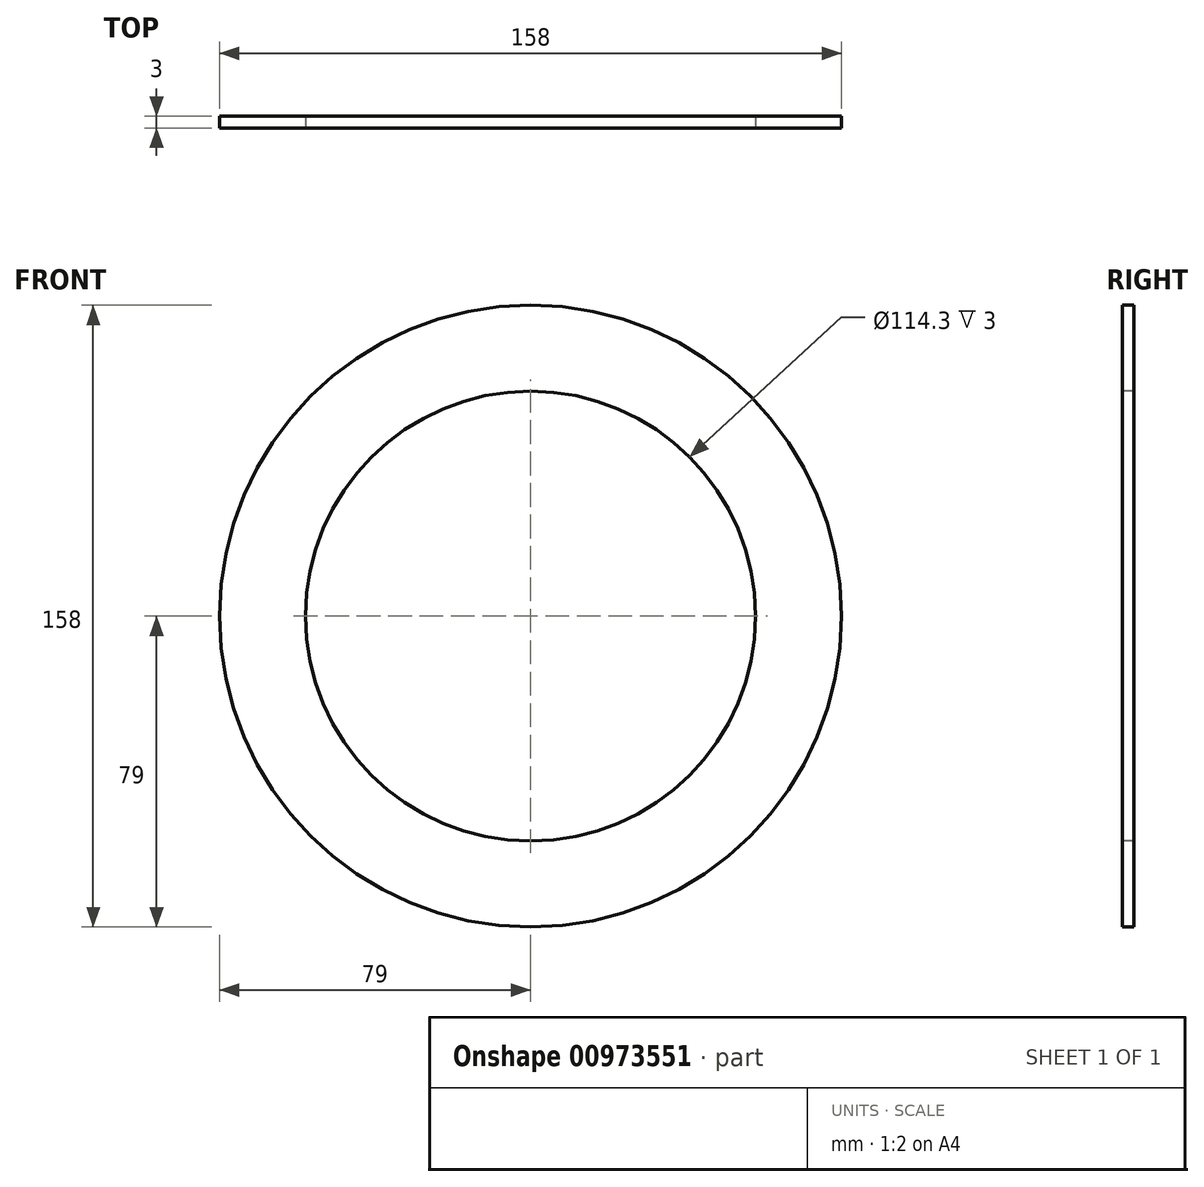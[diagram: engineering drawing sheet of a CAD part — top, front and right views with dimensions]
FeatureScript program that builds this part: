
annotation { "Feature Type Name" : "Feature", "Feature Type Description" : "" }
export const myFeature = defineFeature(function(context is Context, id is Id, definition is map)
    precondition{}
    {
        {
            var Q0;
            Q0=qCreatedBy(makeId("Front.planeOp"),FACE);
            var sketch = newSketch(context, id + "F0", { "sketchPlane" : qUnion([Q0])});
            skCircle(sketch, "E0", {"center": v(0, 0) * mm, "radius": 110 * mm});
            skCircle(sketch, "E1", {"center": v(0, 0) * mm, "radius": 79 * mm});
            skLineSegment(sketch, "E2", {"start": v(0, 0) * mm, "end": v(90, 0) * mm});
            skCircle(sketch, "E3", {"center": v(90, 0) * mm, "radius": 9 * mm});
            skPoint(sketch, "E4.center", {"position": v(41.73, 29.53) * mm});
            skCircle(sketch, "E5.1.0", {"center": v(63.64, 63.64) * mm, "radius": 9 * mm});
            skCircle(sketch, "E5.2.0", {"center": v(0, 90) * mm, "radius": 9 * mm});
            skCircle(sketch, "E5.3.0", {"center": v(-63.64, 63.64) * mm, "radius": 9 * mm});
            skCircle(sketch, "E5.4.0", {"center": v(-90, 0) * mm, "radius": 9 * mm});
            skCircle(sketch, "E5.5.0", {"center": v(-63.64, -63.64) * mm, "radius": 9 * mm});
            skCircle(sketch, "E5.6.0", {"center": v(0, -90) * mm, "radius": 9 * mm});
            skCircle(sketch, "E5.7.0", {"center": v(63.64, -63.64) * mm, "radius": 9 * mm});
            skCircle(sketch, "E6", {"center": v(0, 0) * mm, "radius": 57.15 * mm});
            skSolve(sketch);
        }
        {
            var Q0;
            Q0=makeQuery(id+"F0.imprint","IMPRINT",FACE,{"disambiguationData":[TD([[makeQuery(id+"F0.imprint","IMPRINT",EDGE,{"derivedFrom":sQuery(id+"F0.wireOp",EDGE,"E1")}),1.0]])]});
            var Q1;
            Q1=sQuery(id+"F0.wireOp",EDGE,"E1");
            var Q2;
            Q2=sQuery(id+"F0.wireOp",EDGE,"E6");
            extrude(context, id + "F1", {"entities" : qUnion([Q0]), "surfaceEntities" : qUnion([Q1, Q2]), "oppositeDirection" : true, "depth" : 3 * mm, "offsetDistance" : 25 * mm});
        }
    });
